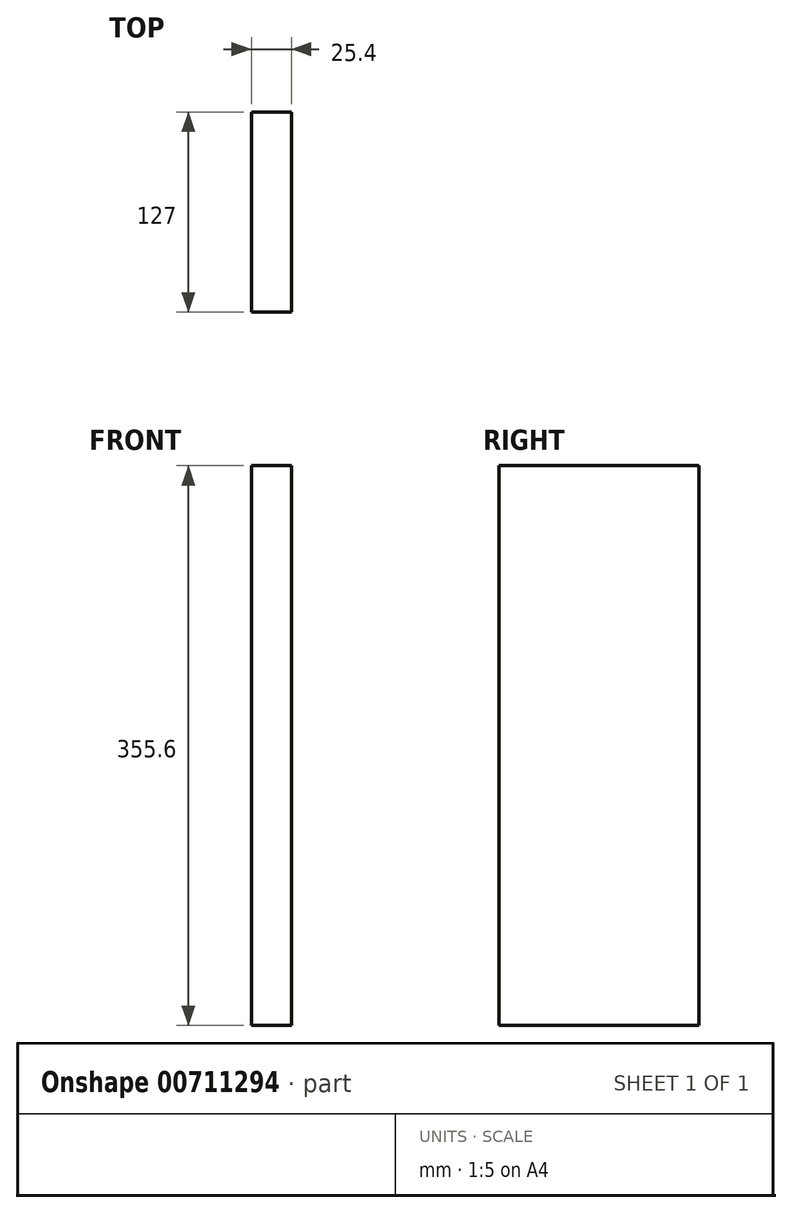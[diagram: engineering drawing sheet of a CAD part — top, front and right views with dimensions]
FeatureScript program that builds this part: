
annotation { "Feature Type Name" : "Feature", "Feature Type Description" : "" }
export const myFeature = defineFeature(function(context is Context, id is Id, definition is map)
    precondition{}
    {
        {
            var Q0;
            Q0=qCreatedBy(makeId("Right.planeOp"),FACE);
            var sketch = newSketch(context, id + "F0", { "sketchPlane" : qUnion([Q0])});
            skLineSegment(sketch, "E0.bottom", {"start": v(-51.96, 297.78) * mm, "end": v(75.04, 297.78) * mm});
            skLineSegment(sketch, "E0.top", {"start": v(-51.96, -57.82) * mm, "end": v(75.04, -57.82) * mm});
            skLineSegment(sketch, "E0.left", {"start": v(-51.96, 297.78) * mm, "end": v(-51.96, -57.82) * mm});
            skLineSegment(sketch, "E0.right", {"start": v(75.04, 297.78) * mm, "end": v(75.04, -57.82) * mm});
            skSolve(sketch);
        }
        {
            var Q0;
            Q0 = qSketchRegion(id + "F0", true);
            extrude(context, id + "F1", {"entities" : qUnion([Q0]), "endBound" : BoundingType.SYMMETRIC, "depth" : 25.4 * mm, "offsetDistance" : 25.4 * mm});
        }
    });
